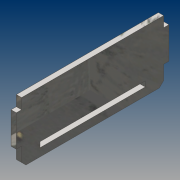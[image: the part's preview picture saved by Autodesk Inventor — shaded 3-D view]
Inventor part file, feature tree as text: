
AUTODESK INVENTOR PART (.ipt)
format: ipt  version: 2021 (Build 250183000, 183)  size: 148,480 bytes
history: native  units: mm
features: extrude x3, sketch x3, projected_geometry x2, chamfer x1
ambient origin geometry x8: Origin, YZ Plane, XZ Plane, XY Plane, X Axis, Y Axis, Z Axis, Center Point
bodies: Solid1 (feature_tree)
feature tree (9):
  extrude  "Extrusion1"  Depth=270.0mm
  extrude  "Extrusion2"  Depth=10.0mm TaperAngle=0.0deg
  extrude  "Extrusion3"  Depth=10.0mm
  chamfer  "Chamfer1"  Distance=60.0mm
  sketch  "Sketch1"  dims[d0=90.0mm d1=270.0mm]
  sketch  "Sketch2"  dims[d2=10.0mm d3=0.0mm d6=10.0mm d7=0.0mm]
  projected_geometry  "Projected Loop1"
  sketch  "Sketch3"  dims[d8=90.0mm d9=50.0mm d10=60.0mm d11=290.0mm d12=270.0mm d13=25.0mm d14=200.0mm d15=10.0mm d16=10.0mm d17=0.0mm d18=8.25mm d19=2.0mm d20=45.0deg]
  projected_geometry  "Projected Loop2"
